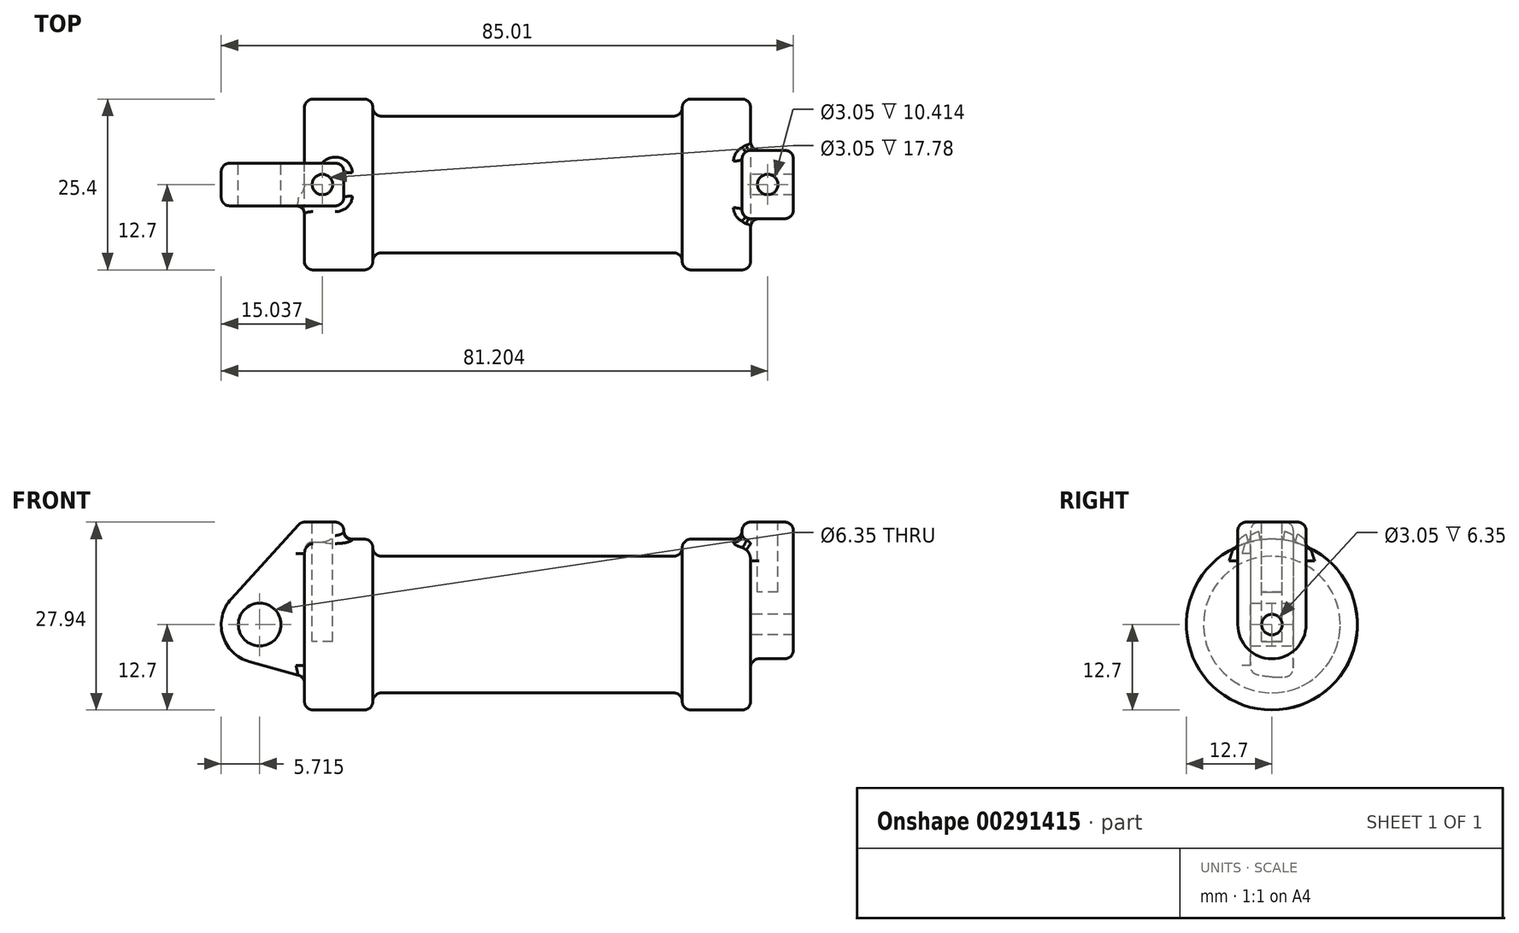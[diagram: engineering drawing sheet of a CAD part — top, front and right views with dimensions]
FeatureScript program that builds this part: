
annotation { "Feature Type Name" : "Feature", "Feature Type Description" : "" }
export const myFeature = defineFeature(function(context is Context, id is Id, definition is map)
    precondition{}
    {
        {
            var Q0;
            Q0=qCreatedBy(makeId("Front.planeOp"),FACE);
            var sketch = newSketch(context, id + "F0", { "sketchPlane" : qUnion([Q0])});
            skLineSegment(sketch, "E0", {"start": v(0, 0) * mm, "end": v(0, 12.7) * mm});
            skLineSegment(sketch, "E1", {"start": v(0, 12.7) * mm, "end": v(10.16, 12.7) * mm});
            skLineSegment(sketch, "E2", {"start": v(10.16, 12.7) * mm, "end": v(10.16, 10.16) * mm});
            skLineSegment(sketch, "E3", {"start": v(10.16, 10.16) * mm, "end": v(56.13, 10.16) * mm});
            skLineSegment(sketch, "E4", {"start": v(56.13, 10.16) * mm, "end": v(56.13, 12.7) * mm});
            skLineSegment(sketch, "E5", {"start": v(56.13, 12.7) * mm, "end": v(66.3, 12.7) * mm});
            skLineSegment(sketch, "E6", {"start": v(66.3, 12.7) * mm, "end": v(66.3, 0) * mm});
            skLineSegment(sketch, "E7", {"start": v(66.3, 0) * mm, "end": v(0, 0) * mm});
            skLineSegment(sketch, "E8", {"start": v(5.84, 15.24) * mm, "end": v(-0.5, 15.24) * mm});
            skLineSegment(sketch, "E9", {"start": v(-0.5, 15.24) * mm, "end": v(-10.88, 3.85) * mm});
            skLineSegment(sketch, "E10", {"start": v(0, 0) * mm, "end": v(-6.65, 0) * mm});
            skCircle(sketch, "E11", {"center": v(-6.65, 0) * mm, "radius": 5.72 * mm});
            skCircle(sketch, "E12", {"center": v(-6.65, 0) * mm, "radius": 3.18 * mm});
            skLineSegment(sketch, "E13", {"start": v(5.84, 15.24) * mm, "end": v(5.84, -9.4) * mm});
            skLineSegment(sketch, "E14", {"start": v(5.84, -9.4) * mm, "end": v(-8.18, -5.5) * mm});
            skSolve(sketch);
        }
        {
            var Q0;
            {var subQ0=sQuery(id+"F0.wireOp",EDGE,"E2");Q0=makeQuery(id+"F0.imprint","IMPRINT",FACE,{"disambiguationData":[TD([[makeQuery(id+"F0.imprint","IMPRINT",EDGE,{"derivedFrom":subQ0}),-1.0]])]});}
            var Q1;
            {var subQ0=sQuery(id+"F0.wireOp",EDGE,"E0");Q1=makeQuery(id+"F0.imprint","IMPRINT",FACE,{"disambiguationData":[TD([[makeQuery(id+"F0.imprint","IMPRINT",EDGE,{"derivedFrom":subQ0}),-1.0]])]});}
            var Q2;
            Q2=sQuery(id+"F0.wireOp",EDGE,"E7");
            revolve(context, id + "F1", {"entities" : qUnion([Q0, Q1]), "axis" : qUnion([Q2]), "revolveType" : RevolveType.FULL});
        }
        {
            var Q0;
            {var subQ0=sQuery(id+"F0.wireOp",EDGE,"E14");Q0=makeQuery(id+"F0.imprint","IMPRINT",FACE,{"disambiguationData":[TD([[makeQuery(id+"F0.imprint","IMPRINT",EDGE,{"derivedFrom":subQ0}),-1.0]])]});}
            var Q1;
            {var subQ1=sQuery(id+"F0.wireOp",EDGE,"E0");Q1=makeQuery(id+"F0.imprint","IMPRINT",FACE,{"disambiguationData":[TD([[makeQuery(id+"F0.imprint","IMPRINT",EDGE,{"derivedFrom":subQ1}),1.0]])]});}
            var Q2;
            {var subQ0=sQuery(id+"F0.wireOp",EDGE,"E0");Q2=makeQuery(id+"F0.imprint","IMPRINT",FACE,{"disambiguationData":[TD([[makeQuery(id+"F0.imprint","IMPRINT",EDGE,{"derivedFrom":subQ0}),-1.0]])]});}
            var Q3;
            {var subQ5=sQuery(id+"F0.wireOp",EDGE,"E12");Q3=makeQuery(id+"F0.imprint","IMPRINT",FACE,{"disambiguationData":[TD([[makeQuery(id+"F0.imprint","IMPRINT",EDGE,{"derivedFrom":subQ5}),-1.0]])]});}
            extrude(context, id + "F2", {"entities" : qUnion([Q0, Q1, Q2, Q3]), "operationType" : NewBodyOperationType.ADD, "endBound" : BoundingType.SYMMETRIC, "depth" : 6.35 * mm});
        }
        {
            var Q0;
            Q0=makeQuery(id+"F1.opRevolve","SWEPT_FACE",FACE,{"disambiguationData":[OSD([sQuery(id+"F0.wireOp",EDGE,"E6")])]});
            var sketch = newSketch(context, id + "F3", { "sketchPlane" : qUnion([Q0])});
            skCircle(sketch, "E15", {"center": v(0, 0) * mm, "radius": 5.08 * mm});
            skCircle(sketch, "E16", {"center": v(0, 0) * mm, "radius": 1.52 * mm});
            skLineSegment(sketch, "E17", {"start": v(-5.08, 0) * mm, "end": v(-5.08, 15.24) * mm});
            skLineSegment(sketch, "E18", {"start": v(-5.08, 15.24) * mm, "end": v(5.08, 15.24) * mm});
            skLineSegment(sketch, "E19", {"start": v(5.08, 15.24) * mm, "end": v(5.08, 0) * mm});
            skSolve(sketch);
        }
        {
            var Q0;
            {var subQ0=sQuery(id+"F3.wireOp",EDGE,"E17");var subQ1=sQuery(id+"F3.wireOp",EDGE,"E15");var subQ2=makeQuery(id+"F3.imprint","INTERSECT",VERTEX,{"derivedFrom":[subQ1,subQ0]});Q0=makeQuery(id+"F3.imprint","IMPRINT",FACE,{"disambiguationData":[TD([[makeQuery(id+"F3.imprint","IMPRINT",EDGE,{"disambiguationData":[TD([[subQ2,1.0]])],"derivedFrom":subQ1}),-1.0]])]});}
            var Q1;
            Q1=makeQuery(id+"F3.imprint","IMPRINT",FACE,{"disambiguationData":[TD([[makeQuery(id+"F3.imprint","IMPRINT",EDGE,{"derivedFrom":sQuery(id+"F3.wireOp",EDGE,"E16")}),-1.0]])]});
            var Q2;
            {var subQ0=sQuery(id+"F3.wireOp",EDGE,"E18");Q2=makeQuery(id+"F3.imprint","IMPRINT",FACE,{"disambiguationData":[TD([[makeQuery(id+"F3.imprint","IMPRINT",EDGE,{"derivedFrom":subQ0}),-1.0]])]});}
            extrude(context, id + "F4", {"entities" : qUnion([Q0, Q1, Q2]), "operationType" : NewBodyOperationType.ADD, "depth" : 6.35 * mm});
        }
        {
            var Q0;
            Q0 = qSketchRegion(id + "F3", true);
            extrude(context, id + "F5", {"entities" : qUnion([Q0]), "operationType" : NewBodyOperationType.ADD, "oppositeDirection" : true, "depth" : 1.27 * mm});
        }
        {
            var Q0;
            {var subQ0=sQuery(id+"F3.wireOp",EDGE,"E18");Q0=makeQuery(id+"F5.boolean.opBoolean","MERGE",FACE,{"derivedFrom":[makeQuery(id+"F4.opExtrude","SWEPT_FACE",FACE,{"disambiguationData":[OSD([subQ0])]}),makeQuery(id+"F5.opExtrude","SWEPT_FACE",FACE,{"disambiguationData":[OSD([subQ0])]})]});}
            var sketch = newSketch(context, id + "F6", { "sketchPlane" : qUnion([Q0])});
            skCircle(sketch, "E20", {"center": v(68.83, 0) * mm, "radius": 1.52 * mm});
            skPoint(sketch, "E20.centerSnap0", {"position": v(65.02, 0) * mm});
            skPoint(sketch, "E20.centerSnap1", {"position": v(68.83, 5.08) * mm});
            skSolve(sketch);
        }
        {
            var Q0;
            Q0 = qSketchRegion(id + "F6", true);
            extrude(context, id + "F7", {"entities" : qUnion([Q0]), "operationType" : NewBodyOperationType.REMOVE, "oppositeDirection" : true, "depth" : 10.4 * mm});
        }
        {
            var Q0;
            Q0=makeQuery(id+"F2.opExtrude","SWEPT_FACE",FACE,{"disambiguationData":[OSD([sQuery(id+"F0.wireOp",EDGE,"E8")])]});
            var sketch = newSketch(context, id + "F8", { "sketchPlane" : qUnion([Q0])});
            skCircle(sketch, "E21", {"center": v(2.67, 0) * mm, "radius": 1.52 * mm});
            skPoint(sketch, "E21.centerSnap0", {"position": v(2.67, 3.18) * mm});
            skPoint(sketch, "E21.centerSnap1", {"position": v(5.84, 0) * mm});
            skSolve(sketch);
        }
        {
            var Q0;
            Q0=makeQuery(id+"F8.imprint","IMPRINT",FACE,{"disambiguationData":[TD([[makeQuery(id+"F8.imprint","IMPRINT",EDGE,{"derivedFrom":sQuery(id+"F8.wireOp",EDGE,"E21")}),1.0]])]});
            extrude(context, id + "F9", {"entities" : qUnion([Q0]), "operationType" : NewBodyOperationType.REMOVE, "oppositeDirection" : true, "depth" : 17.78 * mm});
        }
        {
            var Q0;
            Q0=makeQuery(id+"F1.opRevolve","SWEPT_EDGE",EDGE,{"disambiguationData":[OSD([sQuery(id+"F0.wireOp",EDGE,"E1"),sQuery(id+"F0.wireOp",EDGE,"E2")])]});
            var Q1;
            Q1=makeQuery(id+"F1.opRevolve","SWEPT_EDGE",EDGE,{"disambiguationData":[OSD([sQuery(id+"F0.wireOp",EDGE,"E0"),sQuery(id+"F0.wireOp",EDGE,"E1")])]});
            var Q2;
            Q2=makeQuery(id+"F1.opRevolve","SWEPT_FACE",FACE,{"disambiguationData":[OSD([sQuery(id+"F0.wireOp",EDGE,"E3")])]});
            var Q3;
            Q3=makeQuery(id+"F1.opRevolve","SWEPT_EDGE",EDGE,{"disambiguationData":[OSD([sQuery(id+"F0.wireOp",EDGE,"E4"),sQuery(id+"F0.wireOp",EDGE,"E5")])]});
            var Q4;
            {var subQ0=sQuery(id+"F0.wireOp",EDGE,"E5");var subQ1=sQuery(id+"F0.wireOp",EDGE,"E6");Q4=makeQuery(id+"F4.boolean.opBoolean","SPLIT",EDGE,{"disambiguationData":[topologyDisambiguationEdgeConnected([makeQuery(id+"F1.opRevolve","SWEPT_FACE",FACE,{"disambiguationData":[OSD([subQ1])]})])],"derivedFrom":makeQuery(id+"F1.opRevolve","SWEPT_EDGE",EDGE,{"disambiguationData":[OSD([subQ0,subQ1])]})});}
            fillet(context, id + "F10", {"entities" : qUnion([Q0, Q1, Q2, Q3, Q4]), "radius" : 1.27 * mm, "tangentPropagation" : true, "allowEdgeOverflow" : false});
        }
        {
            var Q0;
            Q0=makeQuery(id+"F2.opExtrude","SWEPT_FACE",FACE,{"disambiguationData":[OSD([sQuery(id+"F0.wireOp",EDGE,"E9")])]});
            var Q1;
            Q1=makeQuery(id+"F2.boolean.opBoolean","INTERSECT",EDGE,{"derivedFrom":[makeQuery(id+"F1.opRevolve","SWEPT_FACE",FACE,{"disambiguationData":[OSD([sQuery(id+"F0.wireOp",EDGE,"E0")])]}),makeQuery(id+"F2.opExtrude","CAP_FACE",FACE,{"disambiguationData":[OSD([sQuery(id+"F0.wireOp",EDGE,"E8"),sQuery(id+"F0.wireOp",EDGE,"E9"),sQuery(id+"F0.wireOp",EDGE,"E11"),sQuery(id+"F0.wireOp",EDGE,"E12"),sQuery(id+"F0.wireOp",EDGE,"E13"),sQuery(id+"F0.wireOp",EDGE,"E14")])],"isStart":false})]});
            var Q2;
            Q2=makeQuery(id+"F2.opExtrude","CAP_EDGE",EDGE,{"disambiguationData":[OSD([sQuery(id+"F0.wireOp",EDGE,"E8")])],"isStart":false});
            var Q3;
            Q3=makeQuery(id+"F2.opExtrude","SWEPT_EDGE",EDGE,{"disambiguationData":[OSD([sQuery(id+"F0.wireOp",EDGE,"E8"),sQuery(id+"F0.wireOp",EDGE,"E13")])]});
            var Q4;
            Q4=makeQuery(id+"F2.opExtrude","CAP_EDGE",EDGE,{"disambiguationData":[OSD([sQuery(id+"F0.wireOp",EDGE,"E8")])],"isStart":true});
            var Q5;
            Q5=makeQuery(id+"F2.opExtrude","SWEPT_FACE",FACE,{"disambiguationData":[OSD([sQuery(id+"F0.wireOp",EDGE,"E13")])]});
            var Q6;
            Q6=makeQuery(id+"F4.opExtrude","CAP_EDGE",EDGE,{"disambiguationData":[OSD([sQuery(id+"F3.wireOp",EDGE,"E17")])],"isStart":false});
            var Q7;
            Q7=makeQuery(id+"F4.opExtrude","CAP_EDGE",EDGE,{"disambiguationData":[OSD([sQuery(id+"F3.wireOp",EDGE,"E18")])],"isStart":false});
            var Q8;
            {var subQ0=sQuery(id+"F3.wireOp",EDGE,"E18");var subQ1=sQuery(id+"F3.wireOp",EDGE,"E17");Q8=makeQuery(id+"F5.boolean.opBoolean","MERGE",EDGE,{"derivedFrom":[makeQuery(id+"F4.opExtrude","SWEPT_EDGE",EDGE,{"disambiguationData":[OSD([subQ1,subQ0])]}),makeQuery(id+"F5.opExtrude","SWEPT_EDGE",EDGE,{"disambiguationData":[OSD([subQ1,subQ0])]})]});}
            var Q9;
            {var subQ0=sQuery(id+"F3.wireOp",EDGE,"E17");Q9=makeQuery(id+"F4.boolean.opBoolean","SPLIT",EDGE,{"disambiguationData":[topologyDisambiguationEdgeConnected([makeQuery(id+"F1.opRevolve","SWEPT_FACE",FACE,{"disambiguationData":[OSD([sQuery(id+"F0.wireOp",EDGE,"E6")])]})])],"derivedFrom":makeQuery(id+"F4.opExtrude","CAP_EDGE",EDGE,{"disambiguationData":[OSD([subQ0])],"isStart":true})});}
            var Q10;
            Q10=makeQuery(id+"F5.opExtrude","CAP_EDGE",EDGE,{"disambiguationData":[OSD([sQuery(id+"F3.wireOp",EDGE,"E18")])],"isStart":false});
            var Q11;
            {var subQ0=sQuery(id+"F3.wireOp",EDGE,"E19");var subQ1=sQuery(id+"F3.wireOp",EDGE,"E18");Q11=makeQuery(id+"F5.boolean.opBoolean","MERGE",EDGE,{"derivedFrom":[makeQuery(id+"F4.opExtrude","SWEPT_EDGE",EDGE,{"disambiguationData":[OSD([subQ1,subQ0])]}),makeQuery(id+"F5.opExtrude","SWEPT_EDGE",EDGE,{"disambiguationData":[OSD([subQ1,subQ0])]})]});}
            var Q12;
            Q12=makeQuery(id+"F5.boolean.opBoolean","INTERSECT",EDGE,{"derivedFrom":[makeQuery(id+"F1.opRevolve","SWEPT_FACE",FACE,{"disambiguationData":[OSD([sQuery(id+"F0.wireOp",EDGE,"E5")])]}),makeQuery(id+"F5.opExtrude","CAP_FACE",FACE,{"disambiguationData":[OSD([sQuery(id+"F3.wireOp",EDGE,"E15"),sQuery(id+"F3.wireOp",EDGE,"E16"),sQuery(id+"F3.wireOp",EDGE,"E17"),sQuery(id+"F3.wireOp",EDGE,"E18"),sQuery(id+"F3.wireOp",EDGE,"E19")])],"isStart":false})]});
            var Q13;
            Q13=makeQuery(id+"F5.opExtrude","CAP_FACE",FACE,{"disambiguationData":[OSD([sQuery(id+"F3.wireOp",EDGE,"E15"),sQuery(id+"F3.wireOp",EDGE,"E16"),sQuery(id+"F3.wireOp",EDGE,"E17"),sQuery(id+"F3.wireOp",EDGE,"E18"),sQuery(id+"F3.wireOp",EDGE,"E19")])],"isStart":false});
            fillet(context, id + "F11", {"entities" : qUnion([Q0, Q1, Q2, Q3, Q4, Q5, Q6, Q7, Q8, Q9, Q10, Q11, Q12, Q13]), "radius" : 1.27 * mm, "tangentPropagation" : true, "allowEdgeOverflow" : false});
        }
    });
